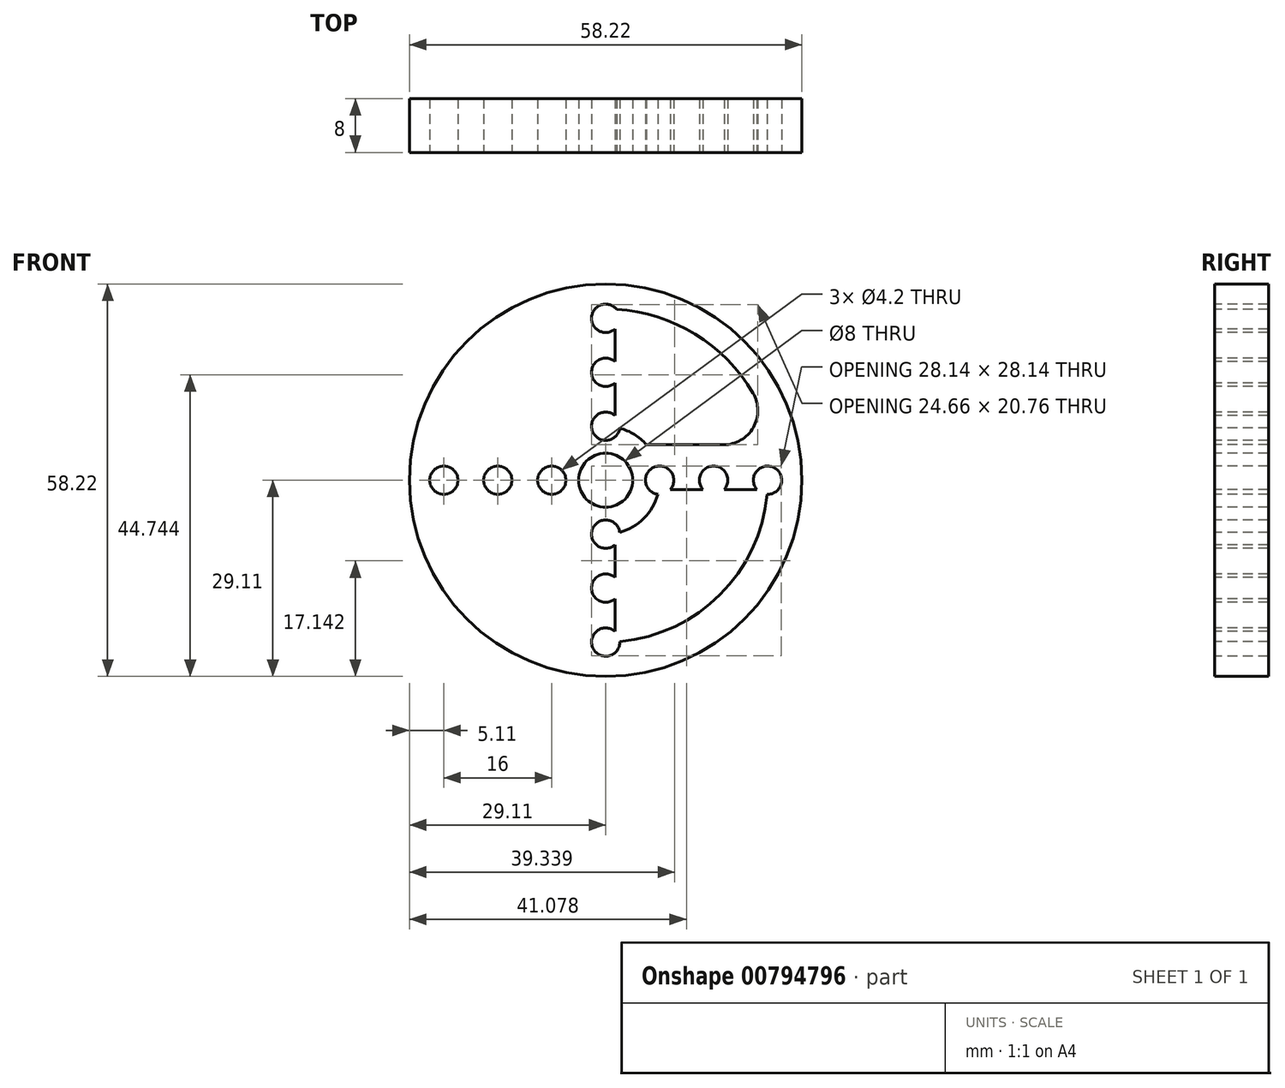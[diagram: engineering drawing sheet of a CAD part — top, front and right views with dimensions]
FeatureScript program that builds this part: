
annotation { "Feature Type Name" : "Feature", "Feature Type Description" : "" }
export const myFeature = defineFeature(function(context is Context, id is Id, definition is map)
    precondition{}
    {
        {
            var Q0;
            Q0=qCreatedBy(makeId("Front.planeOp"),FACE);
            var sketch = newSketch(context, id + "F0", { "sketchPlane" : qUnion([Q0])});
            skCircle(sketch, "E0", {"center": v(0, 0) * mm, "radius": 29.1 * mm});
            skCircle(sketch, "E1", {"center": v(0, 0) * mm, "radius": 4 * mm});
            skCircle(sketch, "E2", {"center": v(0, 0) * mm, "radius": 24 * mm});
            skPoint(sketch, "E3", {"position": v(0, 24) * mm});
            skPoint(sketch, "E4", {"position": v(0, -24) * mm});
            skPoint(sketch, "E5", {"position": v(-24, 0) * mm});
            skPoint(sketch, "E6", {"position": v(24, 0) * mm});
            skCircle(sketch, "E7", {"center": v(0, 0) * mm, "radius": 16 * mm});
            skPoint(sketch, "E8", {"position": v(0, 16) * mm});
            skPoint(sketch, "E9", {"position": v(16, 0) * mm});
            skPoint(sketch, "E10", {"position": v(0, -16) * mm});
            skPoint(sketch, "E11", {"position": v(-16, 0) * mm});
            skCircle(sketch, "E12", {"center": v(0, 0) * mm, "radius": 8 * mm});
            skPoint(sketch, "E13", {"position": v(0, 8) * mm});
            skPoint(sketch, "E14", {"position": v(8, 0) * mm});
            skPoint(sketch, "E15", {"position": v(0, -8) * mm});
            skPoint(sketch, "E16", {"position": v(-8, 0) * mm});
            skCircle(sketch, "E17", {"center": v(0, 0) * mm, "radius": 25.39 * mm});
            skLineSegment(sketch, "E18", {"start": v(1.37, 25.35) * mm, "end": v(1.37, 5.26) * mm});
            skLineSegment(sketch, "E19", {"start": v(1.37, 5.26) * mm, "end": v(24.84, 5.26) * mm});
            skLineSegment(sketch, "E20.MirrorCS", {"start": v(1.37, -25.35) * mm, "end": v(1.37, -1.37) * mm});
            skLineSegment(sketch, "E21.MirrorCS", {"start": v(1.37, -1.37) * mm, "end": v(24.84, -1.37) * mm});
            skSolve(sketch);
        }
        {
            var Q0;
            {var subQ0=sQuery(id+"F0.wireOp",EDGE,"E18");var subQ1=sQuery(id+"F0.wireOp",EDGE,"E7");var subQ2=makeQuery(id+"F0.imprint","INTERSECT",VERTEX,{"derivedFrom":[subQ1,subQ0]});Q0=makeQuery(id+"F0.imprint","IMPRINT",FACE,{"disambiguationData":[TD([[makeQuery(id+"F0.imprint","IMPRINT",EDGE,{"disambiguationData":[TD([[subQ2,-1.0]])],"derivedFrom":subQ1}),1.0]])]});}
            var Q1;
            Q1=makeQuery(id+"F0.imprint","IMPRINT",FACE,{"disambiguationData":[TD([[makeQuery(id+"F0.imprint","IMPRINT",EDGE,{"derivedFrom":sQuery(id+"F0.wireOp",EDGE,"E0")}),1.0]])]});
            var Q2;
            Q2=makeQuery(id+"F0.imprint","IMPRINT",FACE,{"disambiguationData":[TD([[makeQuery(id+"F0.imprint","IMPRINT",EDGE,{"derivedFrom":sQuery(id+"F0.wireOp",EDGE,"E1")}),-1.0]])]});
            var Q3;
            {var subQ0=sQuery(id+"F0.wireOp",EDGE,"E18");var subQ1=sQuery(id+"F0.wireOp",EDGE,"E2");var subQ2=makeQuery(id+"F0.imprint","INTERSECT",VERTEX,{"derivedFrom":[subQ1,subQ0]});Q3=makeQuery(id+"F0.imprint","IMPRINT",FACE,{"disambiguationData":[TD([[makeQuery(id+"F0.imprint","IMPRINT",EDGE,{"disambiguationData":[TD([[subQ2,-1.0]])],"derivedFrom":subQ1}),-1.0]])]});}
            var Q4;
            {var subQ0=sQuery(id+"F0.wireOp",EDGE,"E18");var subQ1=sQuery(id+"F0.wireOp",EDGE,"E2");var subQ2=makeQuery(id+"F0.imprint","INTERSECT",VERTEX,{"derivedFrom":[subQ1,subQ0]});Q4=makeQuery(id+"F0.imprint","IMPRINT",FACE,{"disambiguationData":[TD([[makeQuery(id+"F0.imprint","IMPRINT",EDGE,{"disambiguationData":[TD([[subQ2,-1.0]])],"derivedFrom":subQ1}),1.0]])]});}
            var Q5;
            {var subQ0=sQuery(id+"F0.wireOp",EDGE,"E19");var subQ1=sQuery(id+"F0.wireOp",EDGE,"E7");var subQ2=makeQuery(id+"F0.imprint","INTERSECT",VERTEX,{"derivedFrom":[subQ1,subQ0]});Q5=makeQuery(id+"F0.imprint","IMPRINT",FACE,{"disambiguationData":[TD([[makeQuery(id+"F0.imprint","IMPRINT",EDGE,{"disambiguationData":[TD([[subQ2,1.0]])],"derivedFrom":subQ1}),1.0]])]});}
            var Q6;
            {var subQ0=sQuery(id+"F0.wireOp",EDGE,"E19");var subQ1=sQuery(id+"F0.wireOp",EDGE,"E2");var subQ2=makeQuery(id+"F0.imprint","INTERSECT",VERTEX,{"derivedFrom":[subQ1,subQ0]});Q6=makeQuery(id+"F0.imprint","IMPRINT",FACE,{"disambiguationData":[TD([[makeQuery(id+"F0.imprint","IMPRINT",EDGE,{"disambiguationData":[TD([[subQ2,1.0]])],"derivedFrom":subQ1}),1.0]])]});}
            var Q7;
            {var subQ0=sQuery(id+"F0.wireOp",EDGE,"E19");var subQ1=sQuery(id+"F0.wireOp",EDGE,"E2");var subQ2=makeQuery(id+"F0.imprint","INTERSECT",VERTEX,{"derivedFrom":[subQ1,subQ0]});Q7=makeQuery(id+"F0.imprint","IMPRINT",FACE,{"disambiguationData":[TD([[makeQuery(id+"F0.imprint","IMPRINT",EDGE,{"disambiguationData":[TD([[subQ2,1.0]])],"derivedFrom":subQ1}),-1.0]])]});}
            var Q8;
            {var subQ6=sQuery(id+"F0.wireOp",EDGE,"E1");var subQ10=sQuery(id+"F0.wireOp",EDGE,"E20.MirrorCS");var subQ12=makeQuery(id+"F0.imprint","INTERSECT",VERTEX,{"derivedFrom":[subQ6,subQ10]});Q8=makeQuery(id+"F0.imprint","IMPRINT",FACE,{"disambiguationData":[TD([[makeQuery(id+"F0.imprint","IMPRINT",EDGE,{"disambiguationData":[TD([[subQ12,1.0]])],"derivedFrom":subQ6}),-1.0]])]});}
            var Q9;
            {var subQ0=sQuery(id+"F0.wireOp",EDGE,"E18");var subQ1=sQuery(id+"F0.wireOp",EDGE,"E12");var subQ2=makeQuery(id+"F0.imprint","INTERSECT",VERTEX,{"derivedFrom":[subQ1,subQ0]});Q9=makeQuery(id+"F0.imprint","IMPRINT",FACE,{"disambiguationData":[TD([[makeQuery(id+"F0.imprint","IMPRINT",EDGE,{"disambiguationData":[TD([[subQ2,1.0]])],"derivedFrom":subQ1}),1.0]])]});}
            extrude(context, id + "F1", {"entities" : qUnion([Q0, Q1, Q2, Q3, Q4, Q5, Q6, Q7, Q8, Q9]), "oppositeDirection" : true, "depth" : 8 * mm, "offsetDistance" : 25.4 * mm});
        }
        {
            var Q0;
            Q0=sQuery(id+"F0.wireOp",VERTEX,"E3");
            var Q1;
            Q1=sQuery(id+"F0.wireOp",VERTEX,"E6");
            var Q2;
            Q2=sQuery(id+"F0.wireOp",VERTEX,"E4");
            var Q3;
            Q3=sQuery(id+"F0.wireOp",VERTEX,"E5");
            var Q4;
            Q4=sQuery(id+"F0.wireOp",VERTEX,"E8");
            var Q5;
            Q5=sQuery(id+"F0.wireOp",VERTEX,"E9");
            var Q6;
            Q6=sQuery(id+"F0.wireOp",VERTEX,"E10");
            var Q7;
            Q7=sQuery(id+"F0.wireOp",VERTEX,"E11");
            var Q8;
            Q8=sQuery(id+"F0.wireOp",VERTEX,"E13");
            var Q9;
            Q9=sQuery(id+"F0.wireOp",VERTEX,"E14");
            var Q10;
            Q10=sQuery(id+"F0.wireOp",VERTEX,"E15");
            var Q11;
            Q11=sQuery(id+"F0.wireOp",VERTEX,"E16");
            var Q12;
            Q12=makeQuery(id+"F1.opExtrude","SWEPT_BODY",BODY,{"disambiguationData":[OSD([sQuery(id+"F0.wireOp",EDGE,"E0"),sQuery(id+"F0.wireOp",EDGE,"E1")])]});
            hole(context, id + "F2", {"style" : HoleStyle.SIMPLE, "endStyle" : HoleEndStyle.BLIND, "holeDiameter" : 4.2 * mm, "majorDiameter" : 6.35 * mm, "holeDepth" : 12.7 * mm, "isTappedThrough" : true, "tappedDepth" : 16.94 * mm, "tapClearance" : 3, "startFromSketch" : true, "locations" : qUnion([Q0, Q1, Q2, Q3, Q4, Q5, Q6, Q7, Q8, Q9, Q10, Q11]), "scope" : qUnion([Q12])});
        }
        {
            var Q0;
            Q0=makeQuery(id+"F1.opExtrude","SWEPT_EDGE",EDGE,{"disambiguationData":[OSD([sQuery(id+"F0.wireOp",EDGE,"E17"),sQuery(id+"F0.wireOp",EDGE,"E19")])]});
            fillet(context, id + "F3", {"entities" : qUnion([Q0]), "radius" : 5.08 * mm, "tangentPropagation" : true, "allowEdgeOverflow" : false});
        }
    });
